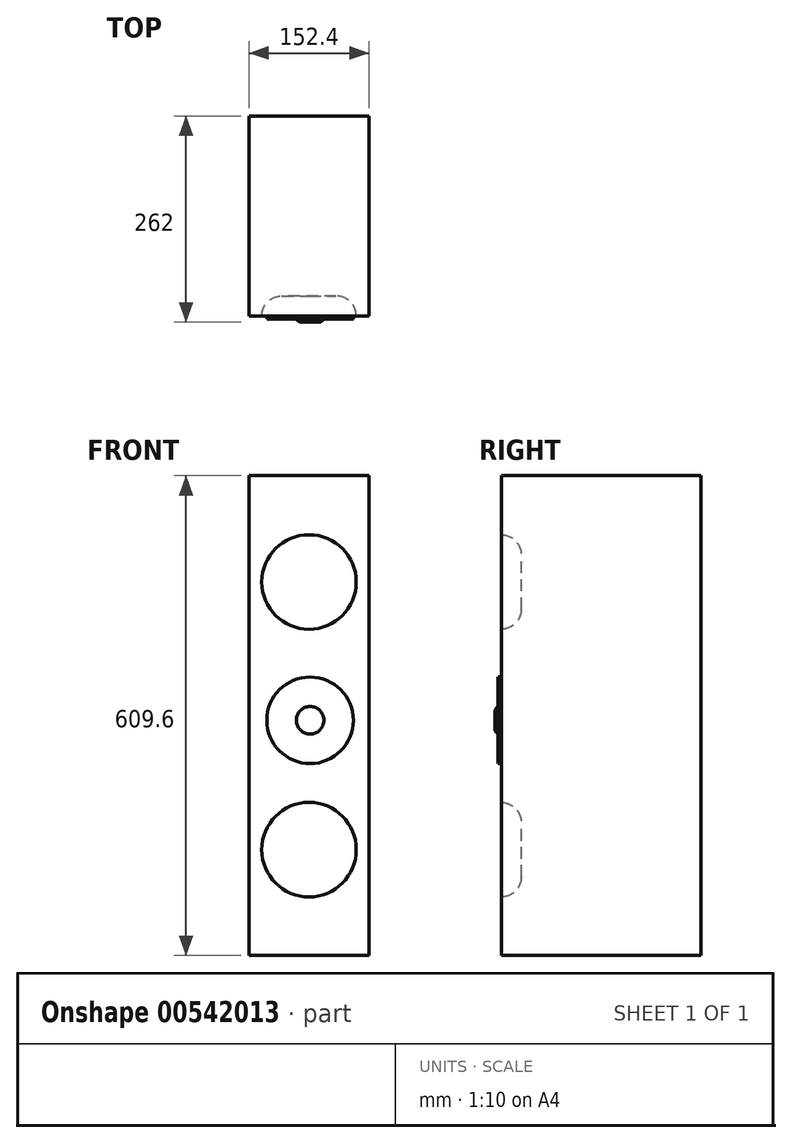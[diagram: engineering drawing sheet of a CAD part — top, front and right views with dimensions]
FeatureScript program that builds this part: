
annotation { "Feature Type Name" : "Feature", "Feature Type Description" : "" }
export const myFeature = defineFeature(function(context is Context, id is Id, definition is map)
    precondition{}
    {
        {
            var Q0;
            Q0=qCreatedBy(makeId("Top.planeOp"),FACE);
            var sketch = newSketch(context, id + "F0", { "sketchPlane" : qUnion([Q0])});
            skLineSegment(sketch, "E0.bottom", {"start": v(0, 254) * mm, "end": v(152.4, 254) * mm});
            skLineSegment(sketch, "E0.top", {"start": v(0, 0) * mm, "end": v(152.4, 0) * mm});
            skLineSegment(sketch, "E0.left", {"start": v(0, 254) * mm, "end": v(0, 0) * mm});
            skLineSegment(sketch, "E0.right", {"start": v(152.4, 254) * mm, "end": v(152.4, 0) * mm});
            skSolve(sketch);
        }
        {
            var Q0;
            Q0=makeQuery(id+"F0.imprint","IMPRINT",FACE,{"disambiguationData":[TD([[makeQuery(id+"F0.imprint","IMPRINT",EDGE,{"derivedFrom":sQuery(id+"F0.wireOp",EDGE,"E0.bottom")}),-1.0]])]});
            extrude(context, id + "F1", {"entities" : qUnion([Q0]), "depth" : 609.6 * mm, "offsetDistance" : 25.4 * mm});
        }
        {
            var Q0;
            Q0=makeQuery(id+"F1.opExtrude","SWEPT_FACE",FACE,{"disambiguationData":[OSD([sQuery(id+"F0.wireOp",EDGE,"E0.top")])]});
            var sketch = newSketch(context, id + "F2", { "sketchPlane" : qUnion([Q0])});
            skCircle(sketch, "E1", {"center": v(76.2, 474.53) * mm, "radius": 60 * mm});
            skCircle(sketch, "E2", {"center": v(76.2, 134.53) * mm, "radius": 60 * mm});
            skCircle(sketch, "E3", {"center": v(77.57, 298.9) * mm, "radius": 55 * mm});
            skCircle(sketch, "E4", {"center": v(77.57, 298.9) * mm, "radius": 17.5 * mm});
            skLineSegment(sketch, "E5.bottom", {"start": v(0, 609.6) * mm, "end": v(152.4, 609.6) * mm});
            skLineSegment(sketch, "E5.top", {"start": v(0, 0) * mm, "end": v(152.4, 0) * mm});
            skLineSegment(sketch, "E5.left", {"start": v(0, 609.6) * mm, "end": v(0, 0) * mm});
            skLineSegment(sketch, "E5.right", {"start": v(152.4, 609.6) * mm, "end": v(152.4, 0) * mm});
            skLineSegment(sketch, "E6", {"start": v(76.2, 609.6) * mm, "end": v(76.2, 0) * mm});
            skSolve(sketch);
        }
        {
            var Q0;
            {var subQ0=sQuery(id+"F2.wireOp",EDGE,"E6");var subQ1=sQuery(id+"F2.wireOp",EDGE,"E1");var subQ2=makeQuery(id+"F2.imprint","INTERSECT",VERTEX,{"disambiguationData":[OD(0.0)],"derivedFrom":[subQ1,subQ0]});Q0=makeQuery(id+"F2.imprint","IMPRINT",FACE,{"disambiguationData":[TD([[makeQuery(id+"F2.imprint","IMPRINT",EDGE,{"disambiguationData":[TD([[subQ2,-1.0]])],"derivedFrom":subQ1}),1.0]])]});}
            var Q1;
            {var subQ0=sQuery(id+"F2.wireOp",EDGE,"E6");var subQ1=sQuery(id+"F2.wireOp",EDGE,"E1");var subQ2=makeQuery(id+"F2.imprint","INTERSECT",VERTEX,{"disambiguationData":[OD(0.0)],"derivedFrom":[subQ1,subQ0]});Q1=makeQuery(id+"F2.imprint","IMPRINT",FACE,{"disambiguationData":[TD([[makeQuery(id+"F2.imprint","IMPRINT",EDGE,{"disambiguationData":[TD([[subQ2,1.0]])],"derivedFrom":subQ1}),1.0]])]});}
            var Q2;
            {var subQ0=sQuery(id+"F2.wireOp",EDGE,"E6");var subQ1=sQuery(id+"F2.wireOp",EDGE,"E2");var subQ2=makeQuery(id+"F2.imprint","INTERSECT",VERTEX,{"disambiguationData":[OD(0.0)],"derivedFrom":[subQ1,subQ0]});Q2=makeQuery(id+"F2.imprint","IMPRINT",FACE,{"disambiguationData":[TD([[makeQuery(id+"F2.imprint","IMPRINT",EDGE,{"disambiguationData":[TD([[subQ2,-1.0]])],"derivedFrom":subQ1}),1.0]])]});}
            var Q3;
            {var subQ0=sQuery(id+"F2.wireOp",EDGE,"E6");var subQ1=sQuery(id+"F2.wireOp",EDGE,"E2");var subQ2=makeQuery(id+"F2.imprint","INTERSECT",VERTEX,{"disambiguationData":[OD(0.0)],"derivedFrom":[subQ1,subQ0]});Q3=makeQuery(id+"F2.imprint","IMPRINT",FACE,{"disambiguationData":[TD([[makeQuery(id+"F2.imprint","IMPRINT",EDGE,{"disambiguationData":[TD([[subQ2,1.0]])],"derivedFrom":subQ1}),1.0]])]});}
            extrude(context, id + "F3", {"entities" : qUnion([Q0, Q1, Q2, Q3]), "operationType" : NewBodyOperationType.REMOVE, "oppositeDirection" : true, "depth" : 25.4 * mm, "offsetDistance" : 25.4 * mm});
        }
        {
            var Q0;
            Q0=makeQuery(id+"F3.boolean.opBoolean","COPY",EDGE,{"derivedFrom":makeQuery(id+"F3.opExtrude","CAP_EDGE",EDGE,{"disambiguationData":[OSD([sQuery(id+"F2.wireOp",EDGE,"E1")])],"isStart":false})});
            var Q1;
            Q1=makeQuery(id+"F3.boolean.opBoolean","COPY",EDGE,{"derivedFrom":makeQuery(id+"F3.opExtrude","CAP_EDGE",EDGE,{"disambiguationData":[OSD([sQuery(id+"F2.wireOp",EDGE,"E2")])],"isStart":false})});
            fillet(context, id + "F4", {"entities" : qUnion([Q0, Q1]), "radius" : 25.4 * mm, "tangentPropagation" : true, "allowEdgeOverflow" : false});
        }
        {
            var Q0;
            {var subQ0=sQuery(id+"F2.wireOp",EDGE,"E6");var subQ1=sQuery(id+"F2.wireOp",EDGE,"E3");var subQ2=makeQuery(id+"F2.imprint","INTERSECT",VERTEX,{"disambiguationData":[OD(0.0)],"derivedFrom":[subQ1,subQ0]});Q0=makeQuery(id+"F2.imprint","IMPRINT",FACE,{"disambiguationData":[TD([[makeQuery(id+"F2.imprint","IMPRINT",EDGE,{"disambiguationData":[TD([[subQ2,1.0]])],"derivedFrom":subQ1}),1.0]])]});}
            var Q1;
            {var subQ0=sQuery(id+"F2.wireOp",EDGE,"E6");var subQ1=sQuery(id+"F2.wireOp",EDGE,"E3");var subQ2=makeQuery(id+"F2.imprint","INTERSECT",VERTEX,{"disambiguationData":[OD(0.0)],"derivedFrom":[subQ1,subQ0]});Q1=makeQuery(id+"F2.imprint","IMPRINT",FACE,{"disambiguationData":[TD([[makeQuery(id+"F2.imprint","IMPRINT",EDGE,{"disambiguationData":[TD([[subQ2,-1.0]])],"derivedFrom":subQ1}),1.0]])]});}
            extrude(context, id + "F5", {"entities" : qUnion([Q0, Q1]), "operationType" : NewBodyOperationType.ADD, "depth" : 4 * mm, "offsetDistance" : 25.4 * mm});
        }
        {
            var Q0;
            {var subQ0=sQuery(id+"F2.wireOp",EDGE,"E6");var subQ1=sQuery(id+"F2.wireOp",EDGE,"E4");var subQ2=makeQuery(id+"F2.imprint","INTERSECT",VERTEX,{"disambiguationData":[OD(0.0)],"derivedFrom":[subQ1,subQ0]});Q0=makeQuery(id+"F2.imprint","IMPRINT",FACE,{"disambiguationData":[TD([[makeQuery(id+"F2.imprint","IMPRINT",EDGE,{"disambiguationData":[TD([[subQ2,1.0]])],"derivedFrom":subQ1}),1.0]])]});}
            var Q1;
            {var subQ0=sQuery(id+"F2.wireOp",EDGE,"E6");var subQ1=sQuery(id+"F2.wireOp",EDGE,"E4");var subQ2=makeQuery(id+"F2.imprint","INTERSECT",VERTEX,{"disambiguationData":[OD(0.0)],"derivedFrom":[subQ1,subQ0]});Q1=makeQuery(id+"F2.imprint","IMPRINT",FACE,{"disambiguationData":[TD([[makeQuery(id+"F2.imprint","IMPRINT",EDGE,{"disambiguationData":[TD([[subQ2,-1.0]])],"derivedFrom":subQ1}),1.0]])]});}
            extrude(context, id + "F6", {"entities" : qUnion([Q0, Q1]), "operationType" : NewBodyOperationType.ADD, "depth" : 8 * mm, "offsetDistance" : 25.4 * mm});
        }
        {
            var Q0;
            Q0=makeQuery(id+"F6.opExtrude","CAP_EDGE",EDGE,{"disambiguationData":[OSD([sQuery(id+"F2.wireOp",EDGE,"E4")])],"isStart":false});
            fillet(context, id + "F7", {"entities" : qUnion([Q0]), "radius" : 8 * mm, "tangentPropagation" : true, "allowEdgeOverflow" : false});
        }
    });
